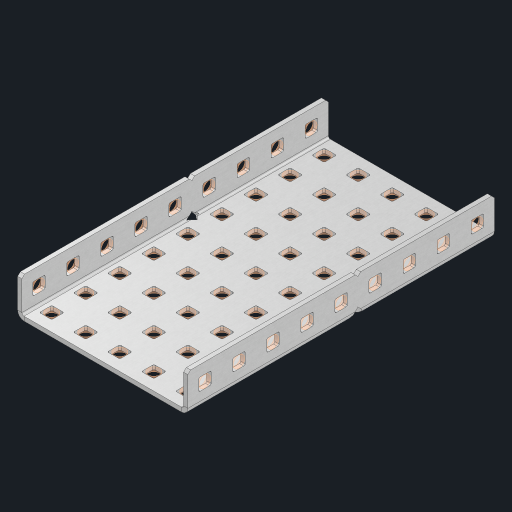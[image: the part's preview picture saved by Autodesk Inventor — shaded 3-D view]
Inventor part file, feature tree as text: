
AUTODESK INVENTOR PART (.ipt)
format: ipt  version: 2023 (Build 270158000, 158)  size: 949,760 bytes
history: native  units: in
note: dims shown in document units (in); Inventor stores cm internally (conversion verified against a paired STEP export)
features: other x68, extrude x62, sheet_metal_op x10, sketch x8, mirror x1, pattern_linear x1, chamfer x1
ambient origin geometry x8: Origin, YZ Plane, XZ Plane, XY Plane, X Axis, Y Axis, Z Axis, Center Point
bodies: Solid1 (feature_tree), Body (feature_tree)
feature tree (151):
  other  "Flange Pattern Plane"
  sheet_metal_op  "Flange Pattern"
  sheet_metal_op  "Body Pattern"
  other  "Arc Length"
  mirror  "Notch Mirror"
  pattern_linear  "Notch Pattern"  Spacing1=0.25in  [1 undecoded]
  chamfer  "End Chamfer"
  extrude  "Half Cut"  Depth=0.0625in
  sketch  "Sketch1"  dims[d0=2.5in]
  other  "Plate1"
  sketch  "Sketch2"  dims[d1=4.5in]
  other  "Plate2"
  sheet_metal_op  "Bend1"
  sheet_metal_op  "Corner1"
  sketch  "Sketch3"  dims[d2=0.0625in]
  other  "Flange Pattern Sketch"
  sketch  "Sketch7"  dims[d3=0.0625in]
  other  "Srf1"
  other  "Srf2"
  sketch  "Sketch8"  dims[d4=0.0312in]
  sketch  "Sketch9"  dims[d5=0.125in]
  other  "Srf91"
  sheet_metal_op  "Body Pattern Sketch"
  other  "Srf92"
  sketch  "Sketch13"  dims[d6=0.0625in]
  sketch  "Sketch14"  dims[d7=0.5in d8=90.0deg d9=0.0312in d10=0.25in d11=0.0625in d12=0.0625in d16=0.182in d17=0.02in d18=0.0625in d19=0.0in d20=0.25in d21=0.25in d46=0.172in d47=1.0in d48=0.0in d49=0.182in d50=0.02in d51=0.25in d52=0.25in d53=0.0625in d54=0.0in d55=0.172in d56=1.0in d57=0.0in d60=3.5433in d62=0.5in d63=1.9685in d65=0.5in d85=0.1473in d86=0.1782in d88=0.04in d89=0.0625in d90=0.0in d91=0.04in d92=0.0491in d95=2.5in d96=0.04in d97=0.25in d98=45.0deg d101=0.0in d102=2.497in d131=2.5in d132=3.5433in d134=0.5in d139=0.5in]
  other  "Srf856"
  other  "Srf1310"
  other  "Srf1311"
  other  "Srf1312"
  other  "Srf1376"
  other  "Srf1377"
  other  "Srf1728"
  other  "Srf1755"
  other  "Srf1878"
  other  "Srf1879"
  other  "Srf1880"
  other  "Srf1881"
  other  "Srf1882"
  other  "Srf1883"
  other  "Srf1884"
  other  "Srf1885"
  other  "Srf1886"
  other  "Srf1887"
  other  "Srf1888"
  other  "Srf1889"
  other  "Srf1942"
  other  "Srf1943"
  other  "Srf1944"
  other  "Srf1945"
  other  "Srf1946"
  other  "Srf1947"
  other  "Srf1948"
  other  "Srf1949"
  other  "Srf1950"
  other  "Srf1951"
  other  "Srf1952"
  other  "Srf1953"
  other  "Srf1954"
  other  "Srf1955"
  other  "Srf1956"
  other  "Srf1957"
  other  "Srf1958"
  other  "Srf1959"
  other  "Srf1960"
  other  "Srf1961"
  other  "Srf1962"
  other  "Srf1963"
  other  "Srf1964"
  other  "Srf1965"
  other  "Srf1966"
  other  "Srf1967"
  other  "Srf1968"
  other  "Srf1969"
  other  "Srf1970"
  other  "Srf2146"
  other  "Srf2147"
  other  "Srf2148"
  other  "Srf2149"
  other  "Srf2150"
  other  "Srf2151"
  other  "Srf2152"
  other  "Srf2153"
  other  "Srf2154"
  other  "Srf2155"
  sheet_metal_op  "Flange Stamp"
  sheet_metal_op  "Flange Circle"
  sheet_metal_op  "Body Stamp"
  sheet_metal_op  "Body Circle"
  sheet_metal_op  "Notch"
  extrude  "ExtrusionSrf2"  Depth=0.0625in
  extrude  "ExtrusionSrf92"  Depth=2.5in
  extrude  "ExtrusionSrf856"  Depth=0.02in
  extrude  "ExtrusionSrf1310"  Depth=0.0625in
  extrude  "ExtrusionSrf1311"  TaperAngle=0.0deg  [1 undecoded]
  extrude  "ExtrusionSrf1312"  Depth=0.25in
  extrude  "ExtrusionSrf1376"  Depth=0.25in
  extrude  "ExtrusionSrf1377"  Depth=2.5in
  extrude  "ExtrusionSrf1728"  Depth=2.5in TaperAngle=0.0deg
  extrude  "ExtrusionSrf1755"  Depth=2.5in
  extrude  "ExtrusionSrf1878"  Depth=0.02in
  extrude  "ExtrusionSrf1879"  Depth=0.25in
  extrude  "ExtrusionSrf1880"  Depth=0.25in
  extrude  "ExtrusionSrf1881"  Depth=0.0625in
  extrude  "ExtrusionSrf1882"  TaperAngle=0.0deg  [1 undecoded]
  extrude  "ExtrusionSrf1883"  Depth=2.5in
  extrude  "ExtrusionSrf1884"  Depth=2.5in TaperAngle=0.0deg
  extrude  "ExtrusionSrf1885"  Depth=2.5in
  extrude  "ExtrusionSrf1886"  Depth=2.5in
  extrude  "ExtrusionSrf1887"  Depth=2.5in
  extrude  "ExtrusionSrf1888"  Depth=2.5in
  extrude  "ExtrusionSrf1889"  Depth=2.5in
  extrude  "ExtrusionSrf1942"  Depth=0.0625in
  extrude  "ExtrusionSrf1943"  TaperAngle=0.0deg  [1 undecoded]
  extrude  "ExtrusionSrf1944"  Depth=2.5in
  extrude  "ExtrusionSrf1945"  Depth=2.5in
  extrude  "ExtrusionSrf1946"  Depth=2.5in
  extrude  "ExtrusionSrf1947"  Depth=0.25in TaperAngle=45.0deg
  extrude  "ExtrusionSrf1948"  TaperAngle=0.0deg  [1 undecoded]
  extrude  "ExtrusionSrf1949"  Depth=2.5in
  extrude  "ExtrusionSrf1950"  Depth=2.5in
  extrude  "ExtrusionSrf1951"  Depth=2.5in
  extrude  "ExtrusionSrf1952"  Depth=2.5in
  extrude  "ExtrusionSrf1953"  Depth=2.5in
  extrude  "ExtrusionSrf1954"  [1 undecoded]
  extrude  "ExtrusionSrf1955"  [1 undecoded]
  extrude  "ExtrusionSrf1956"  [1 undecoded]
  extrude  "ExtrusionSrf1957"  [1 undecoded]
  extrude  "ExtrusionSrf1958"  [1 undecoded]
  extrude  "ExtrusionSrf1959"  [1 undecoded]
  extrude  "ExtrusionSrf1960"  [1 undecoded]
  extrude  "ExtrusionSrf1961"  [1 undecoded]
  extrude  "ExtrusionSrf1962"  [1 undecoded]
  extrude  "ExtrusionSrf1963"  [1 undecoded]
  extrude  "ExtrusionSrf1964"  [1 undecoded]
  extrude  "ExtrusionSrf1965"  [1 undecoded]
  extrude  "ExtrusionSrf1966"  [1 undecoded]
  extrude  "ExtrusionSrf1967"  [1 undecoded]
  extrude  "ExtrusionSrf1968"  [1 undecoded]
  extrude  "ExtrusionSrf1969"  [1 undecoded]
  extrude  "ExtrusionSrf1970"  [1 undecoded]
  extrude  "ExtrusionSrf2146"  [1 undecoded]
  extrude  "ExtrusionSrf2147"  [1 undecoded]
  extrude  "ExtrusionSrf2148"  [1 undecoded]
  extrude  "ExtrusionSrf2149"  [1 undecoded]
  extrude  "ExtrusionSrf2150"  [1 undecoded]
  extrude  "ExtrusionSrf2151"  [1 undecoded]
  extrude  "ExtrusionSrf2152"  [1 undecoded]
  extrude  "ExtrusionSrf2153"  [1 undecoded]
  extrude  "ExtrusionSrf2154"  [1 undecoded]
  extrude  "ExtrusionSrf2155"  [1 undecoded]
note: 32 required parameter values undecoded (feature->parameter linkage not recoverable at this tier; creation-order binding heuristic only, values carry confidence <= 0.55)
